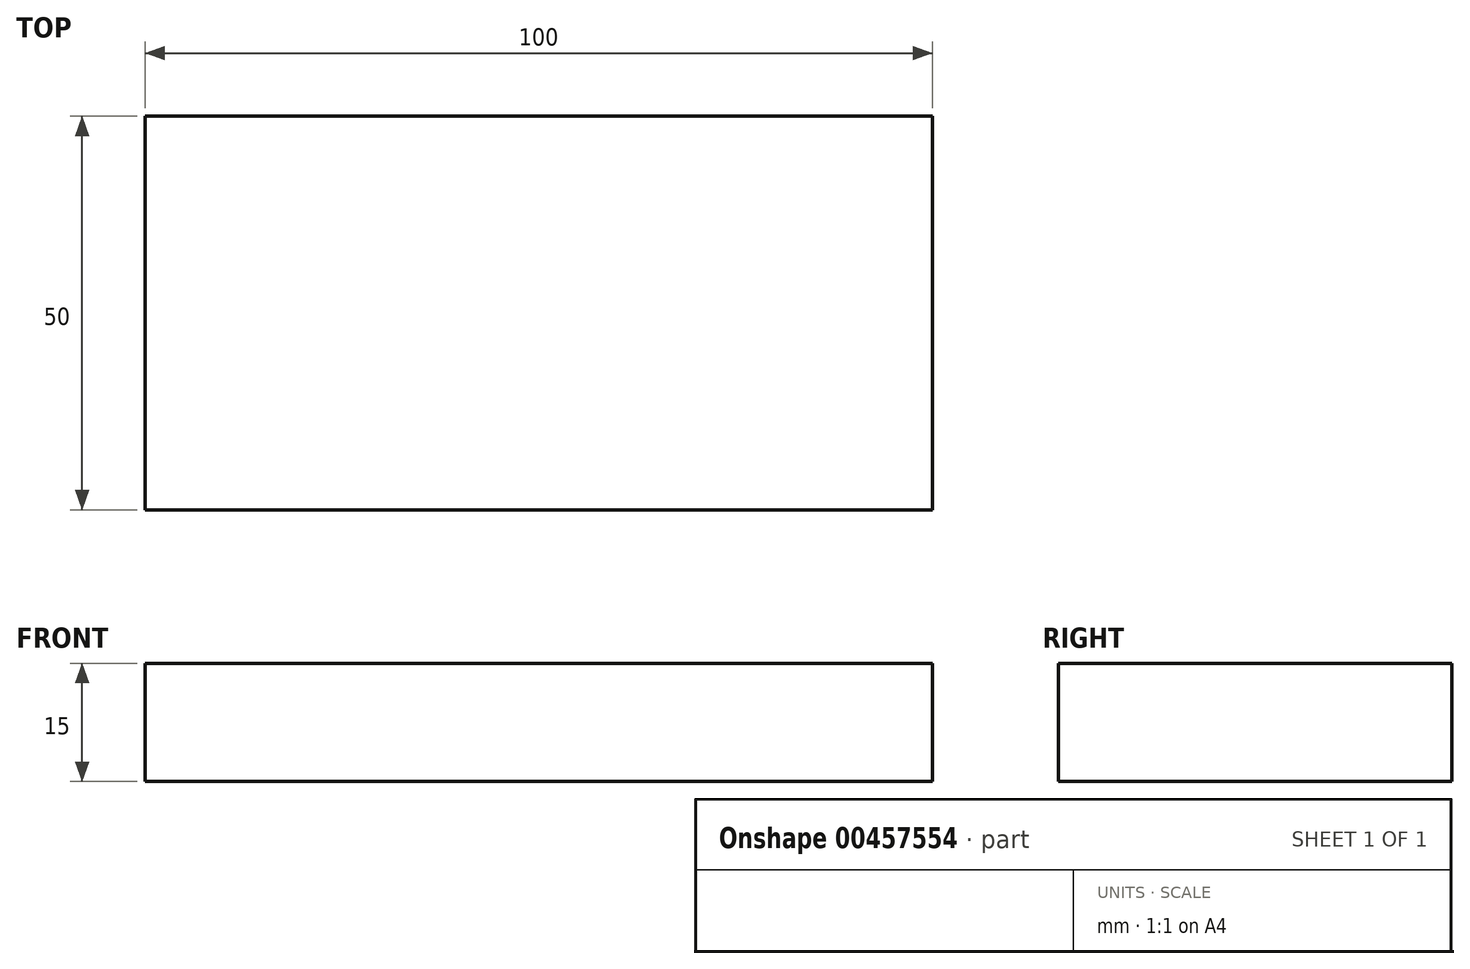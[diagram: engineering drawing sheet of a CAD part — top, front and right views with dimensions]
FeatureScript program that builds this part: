
annotation { "Feature Type Name" : "Feature", "Feature Type Description" : "" }
export const myFeature = defineFeature(function(context is Context, id is Id, definition is map)
    precondition{}
    {
        {
            var Q0;
            Q0=qCreatedBy(makeId("Top.planeOp"),FACE);
            var sketch = newSketch(context, id + "F0", { "sketchPlane" : qUnion([Q0])});
            skLineSegment(sketch, "E0.bottom", {"start": v(0, 0) * mm, "end": v(100, 0) * mm});
            skLineSegment(sketch, "E0.top", {"start": v(0, 50) * mm, "end": v(100, 50) * mm});
            skLineSegment(sketch, "E0.right", {"start": v(100, 0) * mm, "end": v(100, 50) * mm});
            skLineSegment(sketch, "E1", {"start": v(-50, 25) * mm, "end": v(-50, 32.5) * mm});
            skLineSegment(sketch, "E2", {"start": v(-50, 32.5) * mm, "end": v(-50, 25) * mm});
            skLineSegment(sketch, "E3", {"start": v(-50, 25) * mm, "end": v(-50, 17.5) * mm});
            skPoint(sketch, "E4.start.orphan", {"position": v(0, 25) * mm});
            skLineSegment(sketch, "E5", {"start": v(0, 50) * mm, "end": v(0, 0) * mm});
            skSolve(sketch);
        }
        {
            var Q0;
            Q0 = qSketchRegion(id + "F0", true);
            extrude(context, id + "F1", {"entities" : qUnion([Q0]), "depth" : 15 * mm});
        }
        {
            var Q0;
            Q0=makeQuery(id+"F1.opExtrude","SWEPT_FACE",FACE,{"disambiguationData":[OSD([sQuery(id+"F0.wireOp",EDGE,"E5")])]});
            cPlane(context, id + "F2", {"entities" : qUnion([Q0]), "cplaneType" : CPlaneType.OFFSET, "offset" : 50 * mm, "width" : 150 * mm, "height" : 150 * mm});
        }
    });
